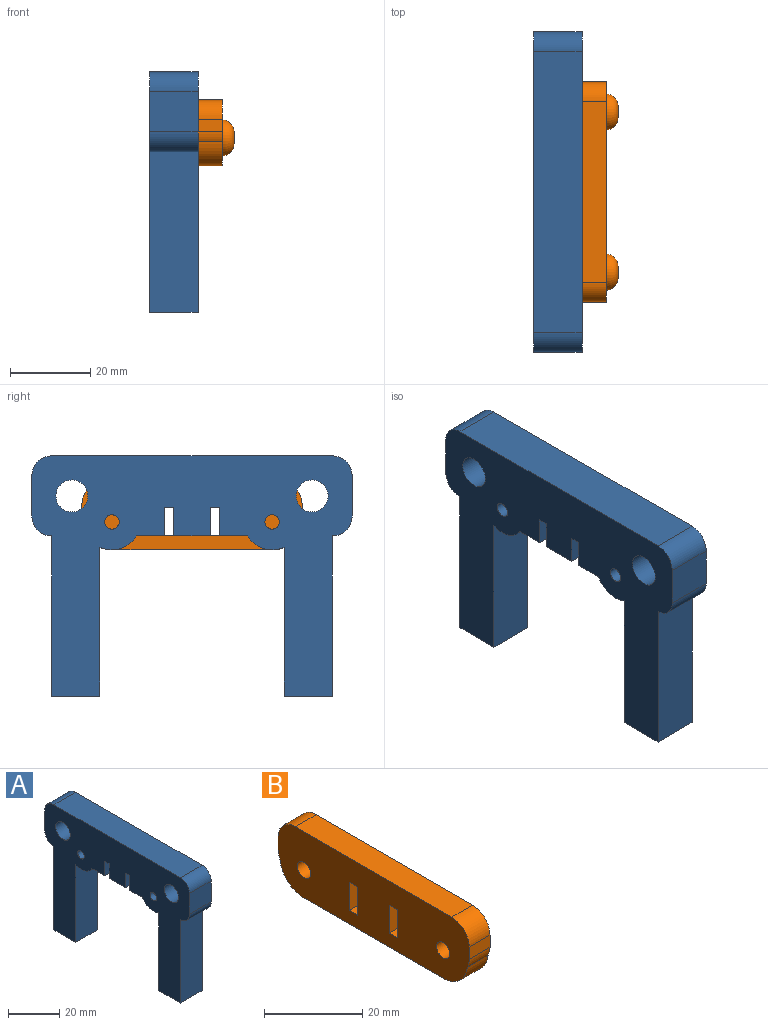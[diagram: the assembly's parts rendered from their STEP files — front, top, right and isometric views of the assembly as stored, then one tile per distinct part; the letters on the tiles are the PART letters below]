
ASSEMBLY  parts=2 mates=1
PART A: 48 faces, bbox 12x80x60 mm
  f0: cylinder r=1.8mm len=9mm, axis (-1,0,0), area 101.8mm2, adj f29,f43
  f1: cylinder r=1.8mm len=9mm, axis (-1,0,0), area 101.8mm2, adj f29,f36
  f2: plane 80x60mm, normal (1,0,0), area 2399.9mm2, adj f3,f4,f5,f6,f7,f8,f9,f10
  f3: cylinder r=5mm len=12mm, axis (-1,0,0), area 94.2mm2, adj f2,f4,f27,f29
  f4: plane 40x12mm, normal (0,-1,0), area 480mm2, adj f2,f3,f5,f29
  f5: plane 12x12mm, normal (0,0,-1), area 131.4mm2, adj f2,f4,f6,f29,f46
  f6: plane 37.18x12mm, normal (0,1,0), area 446.1mm2, adj f2,f5,f7,f29
  f7: cylinder r=7mm len=12mm, axis (-1,0,0), area 125.2mm2, adj f2,f6,f8,f29
  f8: plane 12x7.04mm, normal (0,0,-1), area 84.5mm2, adj f2,f7,f9,f29
  f9: plane 12x7mm, normal (0,1,0), area 84mm2, adj f2,f8,f10,f29
  f10: plane 12x2.4mm, normal (0,0,-1), area 28.8mm2, adj f2,f9,f11,f29
  f11: plane 12x7mm, normal (0,-1,0), area 84mm2, adj f2,f10,f12,f29
  f12: plane 12x9mm, normal (0,0,-1), area 108mm2, adj f2,f11,f13,f29
  f13: plane 12x7mm, normal (0,1,0), area 84mm2, adj f2,f12,f14,f29
  f14: plane 12x2.4mm, normal (0,0,-1), area 28.8mm2, adj f2,f13,f15,f29
  f15: plane 12x7mm, normal (0,-1,0), area 84mm2, adj f2,f14,f16,f29
  f16: plane 12x7.04mm, normal (0,0,-1), area 84.5mm2, adj f2,f15,f17,f29
  f17: cylinder r=7mm len=12mm, axis (-1,0,0), area 125.2mm2, adj f2,f16,f18,f29
  f18: plane 37.18x12mm, normal (0,-1,0), area 446.1mm2, adj f2,f17,f19,f29
  f19: plane 12x12mm, normal (0,0,-1), area 131.4mm2, adj f2,f18,f20,f29,f44
  f20: plane 40x12mm, normal (0,1,0), area 480mm2, adj f2,f19,f21,f29
  f21: cylinder r=5mm len=12mm, axis (-1,0,0), area 94.2mm2, adj f2,f20,f22,f29
  f22: plane 12x10mm, normal (0,1,0), area 120mm2, adj f2,f21,f23,f29
  f23: cylinder r=5mm len=12mm, axis (-1,0,0), area 94.2mm2, adj f2,f22,f24,f29
  f24: plane 70x12mm, normal (0,0,1), area 840mm2, adj f2,f23,f25,f29
  f25: cylinder r=5mm len=12mm, axis (-1,0,0), area 94.2mm2, adj f2,f24,f27,f29
  f26: cylinder r=4mm len=12mm, axis (-1,0,0), area 301.6mm2, adj f2,f29
  f27: plane 12x10mm, normal (0,-1,0), area 120mm2, adj f2,f3,f25,f29
  f28: cylinder r=4mm len=12mm, axis (-1,0,0), area 301.6mm2, adj f2,f29
  f29: plane 80x60mm, normal (-1,0,0), area 2433.8mm2, adj f0,f1,f3,f4,f5,f6,f7,f8
  f30: plane 3x2.8mm, normal (0,0.87,-0.5), area 9.7mm2, adj f2,f31,f35,f36
  f31: plane 3x2.8mm, normal (0,0.87,0.5), area 9.7mm2, adj f2,f30,f32,f36
  f32: plane 3.23x3mm, normal (0,0,1), area 9.7mm2, adj f2,f31,f33,f36
  f33: plane 3x2.8mm, normal (0,-0.87,0.5), area 9.7mm2, adj f2,f32,f34,f36
  f34: plane 3x2.8mm, normal (0,-0.87,-0.5), area 9.7mm2, adj f2,f33,f35,f36
  f35: plane 3.23x3mm, normal (0,0,-1), area 9.7mm2, adj f2,f30,f34,f36
  f36: plane 6.47x5.6mm, normal (1,0,0), area 17mm2, adj f1,f30,f31,f32,f33,f34,f35
  f37: plane 3x2.8mm, normal (0,0.87,-0.5), area 9.7mm2, adj f2,f38,f42,f43
  f38: plane 3x2.8mm, normal (0,0.87,0.5), area 9.7mm2, adj f2,f37,f39,f43
  f39: plane 3.23x3mm, normal (0,0,1), area 9.7mm2, adj f2,f38,f40,f43
  f40: plane 3x2.8mm, normal (0,-0.87,0.5), area 9.7mm2, adj f2,f39,f41,f43
  f41: plane 3x2.8mm, normal (0,-0.87,-0.5), area 9.7mm2, adj f2,f40,f42,f43
  f42: plane 3.23x3mm, normal (0,0,-1), area 9.7mm2, adj f2,f37,f41,f43
  f43: plane 6.47x5.6mm, normal (1,0,0), area 17mm2, adj f0,f37,f38,f39,f40,f41,f42
  f44: cylinder r=2mm len=40mm, axis (0,0,-1), area 502.7mm2, adj f19,f45
  f45: plane 4x4mm, normal (0,0,-1), area 12.6mm2, adj f44
  f46: cylinder r=2mm len=40mm, axis (0,0,-1), area 502.7mm2, adj f5,f47
  f47: plane 4x4mm, normal (0,0,-1), area 12.6mm2, adj f46
PART B: 28 faces, bbox 9x55x16.5 mm
  f0: plane 6x2.4mm, normal (0,0,1), area 14.4mm2, adj f1,f16,f20,f21
  f1: plane 7x6mm, normal (0,1,0), area 42mm2, adj f0,f2,f20,f21
  f2: plane 6x2.4mm, normal (0,0,-1), area 14.4mm2, adj f1,f16,f20,f21
  f3: plane 6x2.4mm, normal (0,0,1), area 14.4mm2, adj f4,f17,f20,f21
  f4: plane 7x6mm, normal (0,1,0), area 42mm2, adj f3,f5,f20,f21
  f5: plane 6x2.4mm, normal (0,0,-1), area 14.4mm2, adj f4,f17,f20,f21
  f6: cylinder r=7mm len=6.87mm, axis (-1,0,0), area 60.9mm2, adj f7,f18,f20,f21
  f7: plane 40.09x6mm, normal (0,0,-1), area 240.5mm2, adj f6,f8,f20,f21
  f8: cylinder r=7mm len=6.96mm, axis (-1,0,0), area 61.4mm2, adj f7,f9,f20,f21
  f9: cylinder r=5mm len=6mm, axis (-1,0,0), area 14.1mm2, adj f8,f10,f20,f21
  f10: plane 6x3mm, normal (0,1,0), area 18mm2, adj f9,f11,f20,f21
  f11: cylinder r=5mm len=6mm, axis (-1,0,0), area 47.1mm2, adj f10,f12,f20,f21
  f12: plane 45x6mm, normal (0,0,1), area 270mm2, adj f11,f13,f20,f21
  f13: cylinder r=5mm len=6mm, axis (-1,0,0), area 47.1mm2, adj f12,f14,f20,f21
  f14: plane 6x3mm, normal (0,-1,0), area 18mm2, adj f13,f18,f20,f21
  f15: cylinder r=1.9mm len=6mm, axis (-1,0,0), area 71.6mm2, adj f21,f25
  f16: plane 7x6mm, normal (0,-1,0), area 42mm2, adj f0,f2,f20,f21
  f17: plane 7x6mm, normal (0,-1,0), area 42mm2, adj f3,f5,f20,f21
  f18: cylinder r=5mm len=6mm, axis (-1,0,0), area 14.1mm2, adj f6,f14,f20,f21
  f19: cylinder r=1.9mm len=6mm, axis (-1,0,0), area 71.6mm2, adj f21,f23
  f20: plane 55x16.5mm, normal (1,0,0), area 707.9mm2, adj f0,f1,f2,f3,f4,f5,f6,f7
  f21: plane 55x16.5mm, normal (-1,0,0), area 812.4mm2, adj f0,f1,f2,f3,f4,f5,f6,f7
  f22: plane 3x3mm, normal (1,0,0), area 7.1mm2, adj f26
  f23: plane 3.8x3.8mm, normal (-1,0,0), area 11.3mm2, adj f19
  f24: plane 3x3mm, normal (1,0,0), area 7.1mm2, adj f27
  f25: plane 3.8x3.8mm, normal (-1,0,0), area 11.3mm2, adj f15
  f26: torus R=1.5mm, axis (1,0,0), area 101mm2, adj f20,f22
  f27: torus R=1.5mm, axis (1,0,0), area 101mm2, adj f20,f24
PLACE A t=(-36.78,15.1,-17.42)mm
PLACE B t=(-30.78,15.1,49.27)mm
MATE fastened B.f21 <-> A.f2  axis (-1,0,0) through (-30.78,8.2,42.77)mm
